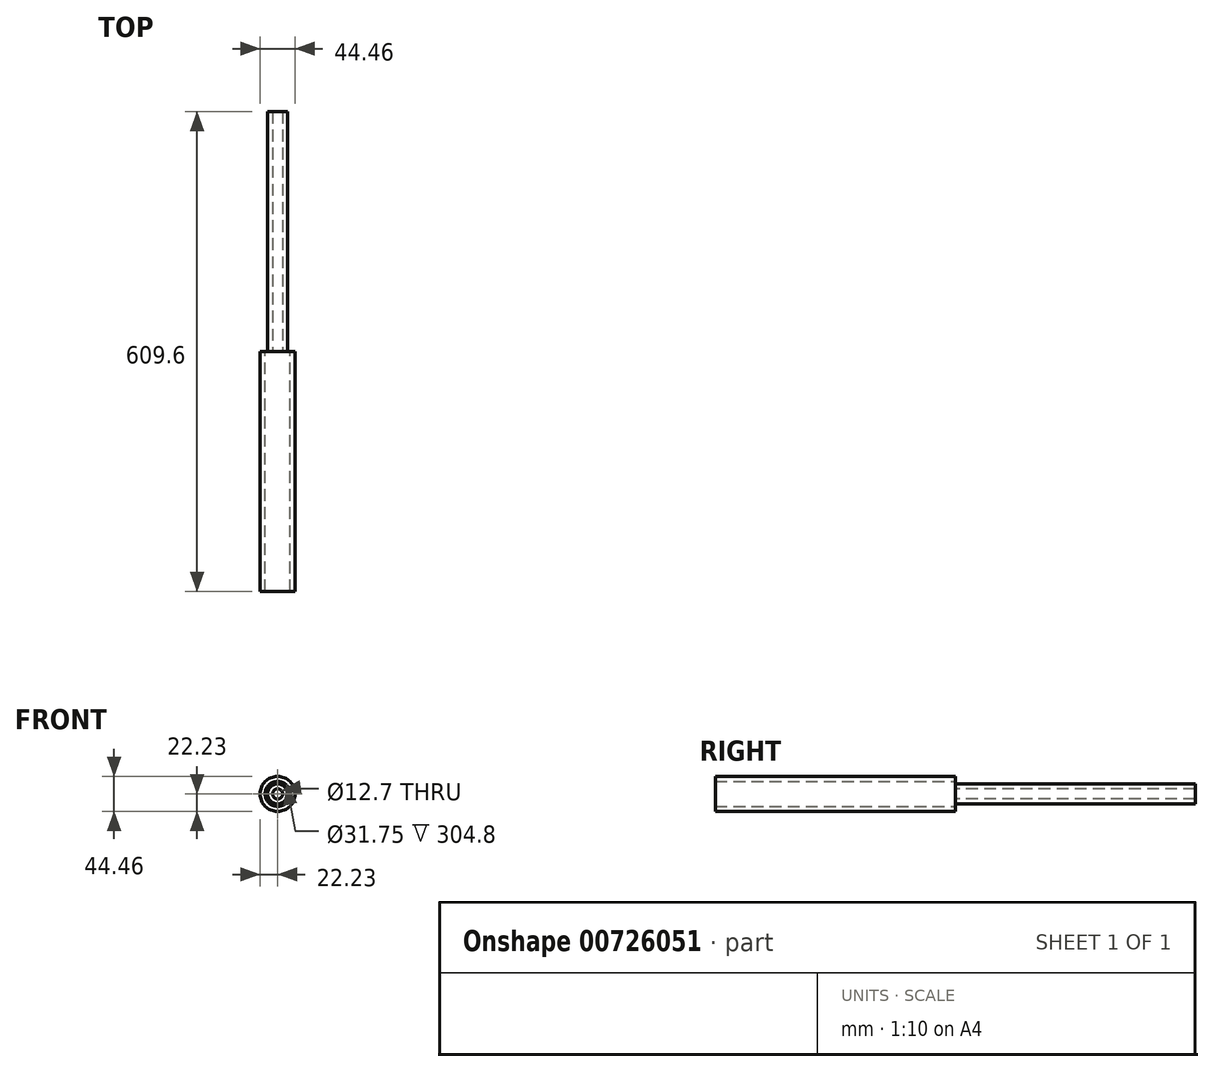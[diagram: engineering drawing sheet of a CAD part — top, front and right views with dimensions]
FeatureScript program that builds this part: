
annotation { "Feature Type Name" : "Feature", "Feature Type Description" : "" }
export const myFeature = defineFeature(function(context is Context, id is Id, definition is map)
    precondition{}
    {
        {
            var Q0;
            Q0=qCreatedBy(makeId("Front.planeOp"),FACE);
            var sketch = newSketch(context, id + "F0", { "sketchPlane" : qUnion([Q0])});
            skCircle(sketch, "E0", {"center": v(0, 0) * mm, "radius": 22.23 * mm});
            skCircle(sketch, "E1", {"center": v(0, 0) * mm, "radius": 15.88 * mm});
            skCircle(sketch, "E2", {"center": v(0, 0) * mm, "radius": 6.35 * mm});
            skCircle(sketch, "E3", {"center": v(0, 0) * mm, "radius": 12.7 * mm});
            skSolve(sketch);
        }
        {
            var Q0;
            Q0=makeQuery(id+"F0.imprint","IMPRINT",FACE,{"disambiguationData":[TD([[makeQuery(id+"F0.imprint","IMPRINT",EDGE,{"derivedFrom":sQuery(id+"F0.wireOp",EDGE,"E0")}),1.0]])]});
            extrude(context, id + "F1", {"entities" : qUnion([Q0]), "depth" : 304.8 * mm, "offsetDistance" : 25.4 * mm});
        }
        {
            var Q0;
            Q0=makeQuery(id+"F0.imprint","IMPRINT",FACE,{"disambiguationData":[TD([[makeQuery(id+"F0.imprint","IMPRINT",EDGE,{"derivedFrom":sQuery(id+"F0.wireOp",EDGE,"E2")}),-1.0]])]});
            extrude(context, id + "F2", {"entities" : qUnion([Q0]), "depth" : -304.8 * mm, "offsetDistance" : 25.4 * mm});
        }
    });
